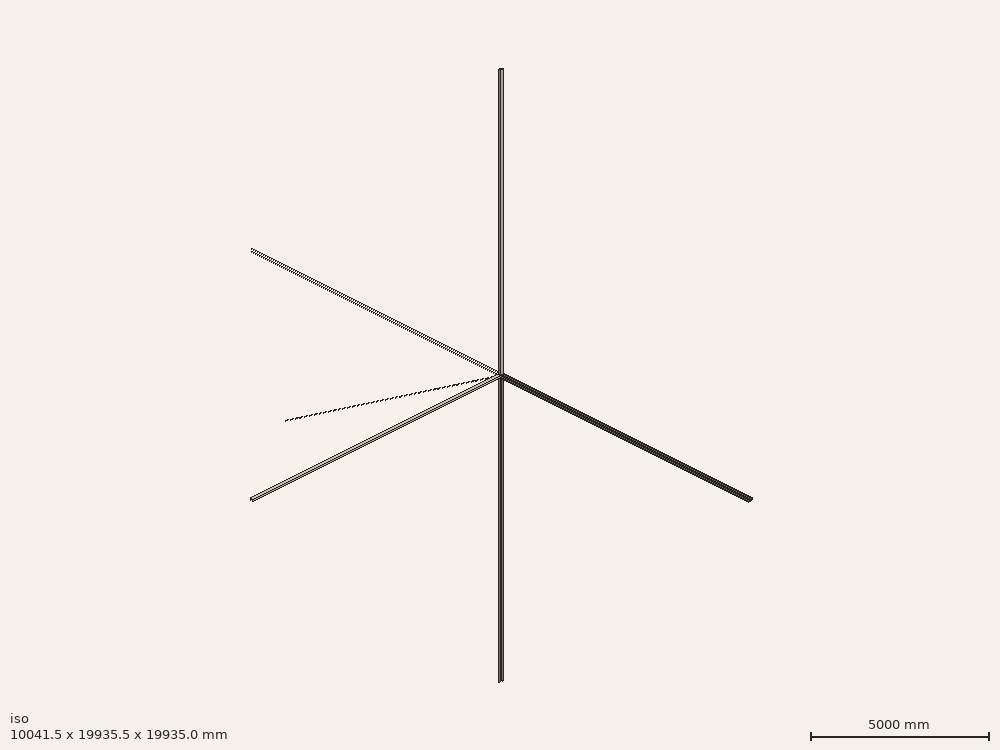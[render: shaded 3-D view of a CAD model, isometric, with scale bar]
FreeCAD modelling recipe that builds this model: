
FCSTD DOCUMENT  (FreeCAD 0.15R4671 (Git))
Label: FullGraphicDisplayBackCover
License: All rights reserved
LicenseURL: http://en.wikipedia.org/wiki/All_rights_reserved
objects: Sketcher::SketchObject×18, PartDesign::Pocket×13, Part::Feature×5, PartDesign::Pad×5, PartDesign::Fillet×5, Mesh::Feature×1
note: 64 computed .brp shape members not serialized (recipe doc carries the construction recipe); baked Part::Feature solids carry a one-line shape summary decoded from their .brp

FEATURE [Mesh::Feature] geetech_graphic_smart_controller
  Placement = pos=(47,-58,-38) rot=(0.447214,-0.447214,0.774597;1.82349rad)
FEATURE [Part::Feature] Part__Feature  label="FrontCover"
  Placement = pos=(0,-37,0) rot=(0,0,1;0rad)
  shape: bbox 100.5 x 70 x 100 mm, 43 faces (baked)
FEATURE [Part::Feature] Part__Feature001  label="OB1515_180mm"
  Placement = pos=(-88,7.5,50) rot=(0,1,0;1.5708rad)
  shape: bbox 180 x 15 x 15 mm, 158 faces (baked)
FEATURE [Part::Feature] Part__Feature002  label="OB1515_180mm001"
  Placement = pos=(-88,7.5,-50) rot=(0,1,0;1.5708rad)
  shape: bbox 180 x 15 x 15 mm, 158 faces (baked)
FEATURE [Sketcher::SketchObject] Sketch
  Placement = pos=(0,0,0) rot=(-1,0,0;4.71239rad)
  sketch-geometry (4):
    g0: LineSegment StartX=-60 StartY=57.5 StartZ=0 EndX=60 EndY=57.5 EndZ=0
    g1: LineSegment StartX=60 StartY=57.5 StartZ=0 EndX=60 EndY=-57.5 EndZ=0
    g2: LineSegment StartX=60 StartY=-57.5 StartZ=0 EndX=-60 EndY=-57.5 EndZ=0
    g3: LineSegment StartX=-60 StartY=-57.5 StartZ=0 EndX=-60 EndY=57.5 EndZ=0
  constraints (12):
    c: Coincident(g0,g1)
    c: Coincident(g1,g2)
    c: Coincident(g2,g3)
    c: Coincident(g3,g0)
    c: Horizontal(g0)
    c: Horizontal(g2)
    c: Vertical(g1)
    c: Vertical(g3)
    c: DistanceY(g1,g0) = 115
    c: DistanceY(g-1,g0) = 57.5
    c: DistanceX(g1,g2) = -120
    c: DistanceX(g-1,g2) = -60
FEATURE [PartDesign::Pad] Pad
  Length = 65
  Length2 = 100
  Placement = pos=(0,0,0) rot=(-1,0,0;4.71239rad)
  Sketch = -> Sketch
  Type = 0
FEATURE [Sketcher::SketchObject] Sketch001
  Placement = pos=(0,-65,0) rot=(1,0,0;1.5708rad)
  Support = -> Pad [Face6]
  sketch-geometry (8):
    g0: LineSegment StartX=50.5 StartY=42.5 StartZ=0 EndX=60.5 EndY=42.5 EndZ=0
    g1: LineSegment StartX=60.5 StartY=42.5 StartZ=0 EndX=60.5 EndY=-42.5 EndZ=0
    g2: LineSegment StartX=60.5 StartY=-42.5 StartZ=0 EndX=50.5 EndY=-42.5 EndZ=0
    g3: LineSegment StartX=50.5 StartY=-42.5 StartZ=0 EndX=50.5 EndY=42.5 EndZ=0
    g4: LineSegment StartX=-60.75 StartY=42.5 StartZ=0 EndX=-50 EndY=42.5 EndZ=0
    g5: LineSegment StartX=-50 StartY=42.5 StartZ=0 EndX=-50 EndY=-42.5 EndZ=0
    g6: LineSegment StartX=-50 StartY=-42.5 StartZ=0 EndX=-60.75 EndY=-42.5 EndZ=0
    g7: LineSegment StartX=-60.75 StartY=-42.5 StartZ=0 EndX=-60.75 EndY=42.5 EndZ=0
  constraints (16):
    c: Coincident(g0,g1)
    c: Coincident(g1,g2)
    c: Coincident(g2,g3)
    c: Coincident(g3,g0)
    c: Horizontal(g0)
    c: Horizontal(g2)
    c: Vertical(g1)
    c: Vertical(g3)
    c: Coincident(g4,g5)
    c: Coincident(g5,g6)
    c: Coincident(g6,g7)
    c: Coincident(g7,g4)
    c: Horizontal(g4)
    c: Horizontal(g6)
    c: Vertical(g5)
    c: Vertical(g7)
FEATURE [PartDesign::Pocket] Pocket
  Length = 5
  Placement = pos=(0,0,0) rot=(-1,0,0;4.71239rad)
  Sketch = -> Sketch001
  Type = 1
FEATURE [Sketcher::SketchObject] Sketch002
  Placement = pos=(60,0,0) rot=(0.707107,0,0.707107;3.14159rad)
  Support = -> Pocket [Face3]
  sketch-geometry (5):
    g0: LineSegment StartX=-50.25 StartY=66.5 StartZ=0 EndX=-50 EndY=65 EndZ=0
    g1: LineSegment StartX=-50 StartY=65 StartZ=0 EndX=50 EndY=7 EndZ=0
    g2: LineSegment StartX=50 StartY=7 StartZ=0 EndX=58.1349 EndY=7 EndZ=0
    g3: LineSegment StartX=58.1349 StartY=7 StartZ=0 EndX=59.3034 EndY=76.0691 EndZ=0
    g4: LineSegment StartX=59.3034 StartY=76.0691 StartZ=0 EndX=-50.25 EndY=66.5 EndZ=0
  constraints (5):
    c: Coincident(g0,g1)
    c: Coincident(g1,g2)
    c: Coincident(g2,g3)
    c: Coincident(g3,g4)
    c: Coincident(g0,g4)
FEATURE [PartDesign::Pocket] Pocket001
  Length = 5
  Placement = pos=(0,0,0) rot=(-1,0,0;4.71239rad)
  Sketch = -> Sketch002
  Type = 1
FEATURE [Sketcher::SketchObject] Sketch003
  Placement = pos=(0,0,57.5) rot=(0,0,1;3.14159rad)
  Support = -> Pocket001 [Face1]
  sketch-geometry (8):
    g0: LineSegment StartX=50 StartY=77.5 StartZ=0 EndX=60.5 EndY=77.5 EndZ=0
    g1: LineSegment StartX=60.5 StartY=77.5 StartZ=0 EndX=60.5 EndY=7 EndZ=0
    g2: LineSegment StartX=60.5 StartY=7 StartZ=0 EndX=50 EndY=7 EndZ=0
    g3: LineSegment StartX=50 StartY=7 StartZ=0 EndX=50 EndY=77.5 EndZ=0
    g4: LineSegment StartX=-61.25 StartY=77.6703 StartZ=0 EndX=-50.5 EndY=77.6703 EndZ=0
    g5: LineSegment StartX=-50.5 StartY=77.6703 StartZ=0 EndX=-50.5 EndY=7 EndZ=0
    g6: LineSegment StartX=-50.5 StartY=7 StartZ=0 EndX=-61.25 EndY=7 EndZ=0
    g7: LineSegment StartX=-61.25 StartY=7 StartZ=0 EndX=-61.25 EndY=77.6703 EndZ=0
  constraints (16):
    c: Coincident(g0,g1)
    c: Coincident(g1,g2)
    c: Coincident(g2,g3)
    c: Coincident(g3,g0)
    c: Horizontal(g0)
    c: Horizontal(g2)
    c: Vertical(g1)
    c: Vertical(g3)
    c: Coincident(g4,g5)
    c: Coincident(g5,g6)
    c: Coincident(g6,g7)
    c: Coincident(g7,g4)
    c: Horizontal(g4)
    c: Horizontal(g6)
    c: Vertical(g5)
    c: Vertical(g7)
FEATURE [PartDesign::Pocket] Pocket002
  Length = 5
  Placement = pos=(0,0,0) rot=(-1,0,0;4.71239rad)
  Sketch = -> Sketch003
  Type = 1
FEATURE [Sketcher::SketchObject] Sketch004
  Placement = pos=(50.5,0,0) rot=(0.707107,0,0.707107;3.14159rad)
  Support = -> Pocket002 [Face17]
  sketch-geometry (4):
    g0: LineSegment StartX=-58 StartY=65.5 StartZ=0 EndX=-50 EndY=65.5 EndZ=0
    g1: LineSegment StartX=-50 StartY=65.5 StartZ=0 EndX=-50 EndY=7 EndZ=0
    g2: LineSegment StartX=-50 StartY=7 StartZ=0 EndX=-58 EndY=7 EndZ=0
    g3: LineSegment StartX=-58 StartY=7 StartZ=0 EndX=-58 EndY=65.5 EndZ=0
  constraints (8):
    c: Coincident(g0,g1)
    c: Coincident(g1,g2)
    c: Coincident(g2,g3)
    c: Coincident(g3,g0)
    c: Horizontal(g0)
    c: Horizontal(g2)
    c: Vertical(g1)
    c: Vertical(g3)
FEATURE [PartDesign::Pocket] Pocket003
  Length = 5
  Placement = pos=(0,0,0) rot=(-1,0,0;4.71239rad)
  Sketch = -> Sketch004
  Type = 1
FEATURE [Sketcher::SketchObject] Sketch005
  Placement = pos=(0,0,0) rot=(-1,0,0;1.5708rad)
  Support = -> Pocket003 [Face2]
  sketch-geometry (4):
    g0: LineSegment StartX=-47 StartY=42.5 StartZ=0 EndX=47.5 EndY=42.5 EndZ=0
    g1: LineSegment StartX=47.5 StartY=42.5 StartZ=0 EndX=47.5 EndY=-42.5 EndZ=0
    g2: LineSegment StartX=47.5 StartY=-42.5 StartZ=0 EndX=-47 EndY=-42.5 EndZ=0
    g3: LineSegment StartX=-47 StartY=-42.5 StartZ=0 EndX=-47 EndY=42.5 EndZ=0
  constraints (8):
    c: Coincident(g0,g1)
    c: Coincident(g1,g2)
    c: Coincident(g2,g3)
    c: Coincident(g3,g0)
    c: Horizontal(g0)
    c: Horizontal(g2)
    c: Vertical(g1)
    c: Vertical(g3)
FEATURE [PartDesign::Pocket] Pocket004
  Length = 5
  Placement = pos=(0,0,0) rot=(-1,0,0;4.71239rad)
  Sketch = -> Sketch005
  Type = 1
FEATURE [Sketcher::SketchObject] Sketch006
  Placement = pos=(47.5,0,0) rot=(0.707107,0,-0.707107;3.14159rad)
  Support = -> Pocket004 [Face18]
  sketch-geometry (4):
    g0: LineSegment StartX=14.7798 StartY=44.7511 StartZ=0 EndX=16.486 EndY=41.7608 EndZ=0
    g1: LineSegment StartX=16.486 StartY=41.7608 StartZ=0 EndX=-7.74724 EndY=27.9339 EndZ=0
    g2: LineSegment StartX=-7.74724 StartY=27.9339 StartZ=0 EndX=-9.45343 EndY=30.9242 EndZ=0
    g3: LineSegment StartX=-9.45343 StartY=30.9242 StartZ=0 EndX=14.7798 EndY=44.7511 EndZ=0
  constraints (7):
    c: Coincident(g0,g1)
    c: Coincident(g1,g2)
    c: Coincident(g2,g3)
    c: Angle(g1,g2) = 1.5708
    c: Angle(g2,g3) = 1.5708
    c: Coincident(g0,g3)
    c: Angle(g3,g0) = 1.5708
FEATURE [PartDesign::Pocket] Pocket005
  Length = 5
  Placement = pos=(0,0,0) rot=(-1,0,0;4.71239rad)
  Sketch = -> Sketch006
  Type = 0
FEATURE [Sketcher::SketchObject] Sketch007
  Placement = pos=(0,0,-42.5) rot=(0,0,1;3.14159rad)
  Support = -> Pocket005 [Face17]
  sketch-geometry (4):
    g0: LineSegment StartX=-45 StartY=60 StartZ=0 EndX=45 EndY=60 EndZ=0
    g1: LineSegment StartX=45 StartY=60 StartZ=0 EndX=45 EndY=73.3448 EndZ=0
    g2: LineSegment StartX=45 StartY=73.3448 StartZ=0 EndX=-45 EndY=73.3448 EndZ=0
    g3: LineSegment StartX=-45 StartY=73.3448 StartZ=0 EndX=-45 EndY=60 EndZ=0
  constraints (8):
    c: Coincident(g0,g1)
    c: Coincident(g1,g2)
    c: Coincident(g2,g3)
    c: Coincident(g3,g0)
    c: Horizontal(g0)
    c: Horizontal(g2)
    c: Vertical(g1)
    c: Vertical(g3)
FEATURE [PartDesign::Pad] Pad001
  Length = 4.3
  Length2 = 100
  Placement = pos=(0,0,0) rot=(-1,0,0;4.71239rad)
  Reversed = true
  Sketch = -> Sketch007
  Type = 0
FEATURE [PartDesign::Fillet] Fillet
  Base = -> Pad001 [Edge92,Edge88]
  Placement = pos=(0,0,0) rot=(-1,0,0;4.71239rad)
  Radius = 2
FEATURE [Sketcher::SketchObject] Sketch008
  Placement = pos=(0,0,0) rot=(-1,0,0;1.5708rad)
  Support = -> Fillet [Face10]
  sketch-geometry (4):
    g0: LineSegment StartX=-49 StartY=44 StartZ=0 EndX=50 EndY=44 EndZ=0
    g1: LineSegment StartX=50 StartY=44 StartZ=0 EndX=50 EndY=-43 EndZ=0
    g2: LineSegment StartX=50 StartY=-43 StartZ=0 EndX=-49 EndY=-43 EndZ=0
    g3: LineSegment StartX=-49 StartY=-43 StartZ=0 EndX=-49 EndY=44 EndZ=0
  constraints (8):
    c: Coincident(g0,g1)
    c: Coincident(g1,g2)
    c: Coincident(g2,g3)
    c: Coincident(g3,g0)
    c: Horizontal(g0)
    c: Horizontal(g2)
    c: Vertical(g1)
    c: Vertical(g3)
FEATURE [PartDesign::Pad] Pad002
  Length = 3
  Length2 = 100
  Placement = pos=(0,0,0) rot=(-1,0,0;4.71239rad)
  Reversed = true
  Sketch = -> Sketch008
  Type = 0
FEATURE [Sketcher::SketchObject] Sketch009
  Placement = pos=(0,-26.938,15.6241) rot=(1,0,0;1.04521rad)
  Support = -> Pad002 [Face4]
  sketch-geometry (10):
    g0: ArcOfCircle CenterX=-43.5 CenterY=25.5 CenterZ=0 NormalX=0 NormalY=0 NormalZ=1 Radius=6 StartAngle=4.71239 EndAngle=6.28319
    g1: ArcOfCircle CenterX=44.5 CenterY=25.5 CenterZ=0 NormalX=0 NormalY=0 NormalZ=1 Radius=6 StartAngle=3.14434 EndAngle=4.70541
    g2: LineSegment StartX=38.5 StartY=25.4835 StartZ=0 EndX=38.5 EndY=36 EndZ=0
    g3: LineSegment StartX=38.5 StartY=36 StartZ=0 EndX=48.5 EndY=36 EndZ=0
    g4: LineSegment StartX=48.5 StartY=36 StartZ=0 EndX=48.5 EndY=19.5 EndZ=0
    g5: LineSegment StartX=48.5 StartY=19.5 StartZ=0 EndX=44.4581 EndY=19.5001 EndZ=0
    g6: LineSegment StartX=-37.5 StartY=25.5 StartZ=0 EndX=-37.5 EndY=37.5 EndZ=0
    g7: LineSegment StartX=-37.5 StartY=37.5 StartZ=0 EndX=-47.5 EndY=37.5 EndZ=0
    g8: LineSegment StartX=-47.5 StartY=37.5 StartZ=0 EndX=-47.5 EndY=19.5 EndZ=0
    g9: LineSegment StartX=-47.5 StartY=19.5 StartZ=0 EndX=-43.5 EndY=19.5 EndZ=0
  constraints (16):
    c: Radius(g0) = 6
    c: Radius(g1) = 6
    c: Coincident(g2,g3)
    c: Coincident(g3,g4)
    c: Coincident(g4,g5)
    c: Coincident(g6,g7)
    c: Coincident(g7,g8)
    c: Coincident(g8,g9)
    c: Coincident(g1,g5)
    c: Coincident(g1,g2)
    c: Coincident(g0,g6)
    c: Coincident(g0,g9)
    c: Horizontal(g7)
    c: Vertical(g8)
    c: Horizontal(g3)
    c: Vertical(g4)
FEATURE [PartDesign::Pad] Pad003
  Length = 20
  Length2 = 100
  Placement = pos=(0,0,0) rot=(-1,0,0;4.71239rad)
  Reversed = true
  Sketch = -> Sketch009
  Type = 0
FEATURE [Sketcher::SketchObject] Sketch010
  Placement = pos=(0,0,57.5) rot=(0,0,1;3.14159rad)
  Support = -> Pad003 [Face29]
  sketch-geometry (4):
    g0: LineSegment StartX=-61 StartY=0 StartZ=0 EndX=61 EndY=0 EndZ=0
    g1: LineSegment StartX=61 StartY=0 StartZ=0 EndX=61 EndY=-16 EndZ=0
    g2: LineSegment StartX=61 StartY=-16 StartZ=0 EndX=-61 EndY=-16 EndZ=0
    g3: LineSegment StartX=-61 StartY=-16 StartZ=0 EndX=-61 EndY=0 EndZ=0
  constraints (8):
    c: Coincident(g0,g1)
    c: Coincident(g1,g2)
    c: Coincident(g2,g3)
    c: Coincident(g3,g0)
    c: Horizontal(g0)
    c: Horizontal(g2)
    c: Vertical(g1)
    c: Vertical(g3)
FEATURE [PartDesign::Pocket] Pocket006
  Length = 5
  Placement = pos=(0,0,0) rot=(-1,0,0;4.71239rad)
  Sketch = -> Sketch010
  Type = 1
FEATURE [Part::Feature] Pocket007
  shape: bbox 120 x 73.36 x 115 mm, 37 faces (baked)
FEATURE [Sketcher::SketchObject] Sketch011
  Placement = pos=(0,-26.938,15.6241) rot=(1,0,0;1.04521rad)
  Support = -> Pocket007 [Face4]
  sketch-geometry (10):
    g0: ArcOfCircle CenterX=-43.5 CenterY=25.5 CenterZ=0 NormalX=0 NormalY=0 NormalZ=1 Radius=6 StartAngle=4.71239 EndAngle=6.28319
    g1: ArcOfCircle CenterX=44.5 CenterY=25.5 CenterZ=0 NormalX=0 NormalY=0 NormalZ=1 Radius=6 StartAngle=3.14159 EndAngle=4.71239
    g2: LineSegment StartX=-43.5 StartY=19.5 StartZ=0 EndX=-47 EndY=19.5 EndZ=0
    g3: LineSegment StartX=-47 StartY=19.5 StartZ=0 EndX=-47 EndY=31 EndZ=0
    g4: LineSegment StartX=-47 StartY=31 StartZ=0 EndX=-37.5 EndY=31 EndZ=0
    g5: LineSegment StartX=-37.5 StartY=31 StartZ=0 EndX=-37.5 EndY=25.5 EndZ=0
    g6: LineSegment StartX=44.5 StartY=19.5 StartZ=0 EndX=47.5 EndY=19.5 EndZ=0
    g7: LineSegment StartX=47.5 StartY=19.5 StartZ=0 EndX=47.5 EndY=31 EndZ=0
    g8: LineSegment StartX=47.5 StartY=31 StartZ=0 EndX=38.5 EndY=31 EndZ=0
    g9: LineSegment StartX=38.5 StartY=31 StartZ=0 EndX=38.5 EndY=25.5 EndZ=0
  constraints (10):
    c: Coincident(g2,g3)
    c: Coincident(g3,g4)
    c: Coincident(g4,g5)
    c: Coincident(g6,g7)
    c: Coincident(g7,g8)
    c: Coincident(g8,g9)
    c: Coincident(g1,g6)
    c: Coincident(g1,g9)
    c: Coincident(g0,g5)
    c: Coincident(g0,g2)
FEATURE [PartDesign::Pad] Pad004
  Length = 4.6
  Length2 = 100
  Sketch = -> Sketch011
  Type = 0
FEATURE [Sketcher::SketchObject] Sketch012
  Placement = pos=(0,-30.9172,17.932) rot=(1,0,0;1.04521rad)
  Support = -> Pad004 [Face30]
  sketch-geometry (2):
    g0: Circle CenterX=-43.5 CenterY=25.5 CenterZ=0 NormalX=0 NormalY=0 NormalZ=1 Radius=1.8
    g1: Circle CenterX=44.5 CenterY=25.5 CenterZ=0 NormalX=0 NormalY=0 NormalZ=1 Radius=1.8
  constraints (2):
    c: Radius(g0) = 1.8
    c: Equal(g0,g1)
FEATURE [PartDesign::Pocket] Pocket008
  Length = 5
  Sketch = -> Sketch012
  Type = 1
FEATURE [Sketcher::SketchObject] Sketch013
  Placement = pos=(0,-26.938,15.6241) rot=(1,0,0;1.04521rad)
  Support = -> Pocket008 [Face4]
  sketch-geometry (2):
    g0: Circle CenterX=-43.5 CenterY=25.5 CenterZ=0 NormalX=0 NormalY=0 NormalZ=1 Radius=3.45
    g1: Circle CenterX=44.5 CenterY=25.5 CenterZ=0 NormalX=0 NormalY=0 NormalZ=1 Radius=3.45
  constraints (2):
    c: Radius(g0) = 3.45
    c: Equal(g0,g1)
FEATURE [PartDesign::Pocket] Pocket009
  Length = 5
  Sketch = -> Sketch013
  Type = 1
FEATURE [Sketcher::SketchObject] Sketch014
  Placement = pos=(0,-7,0) rot=(1,0,0;1.5708rad)
  Support = -> Pocket009 [Face23]
  sketch-geometry (4):
    g0: Circle CenterX=55 CenterY=50 CenterZ=0 NormalX=0 NormalY=0 NormalZ=1 Radius=1.8
    g1: Circle CenterX=-55 CenterY=50 CenterZ=0 NormalX=0 NormalY=0 NormalZ=1 Radius=1.8
    g2: Circle CenterX=55 CenterY=-50 CenterZ=0 NormalX=0 NormalY=0 NormalZ=1 Radius=1.8
    g3: Circle CenterX=-55 CenterY=-50 CenterZ=0 NormalX=0 NormalY=0 NormalZ=1 Radius=1.8
  constraints (4):
    c: Radius(g1) = 1.8
    c: Equal(g1,g0)
    c: Equal(g1,g2)
    c: Equal(g1,g3)
FEATURE [PartDesign::Pocket] Pocket010
  Length = 5
  Sketch = -> Sketch014
  Type = 1
FEATURE [Sketcher::SketchObject] Sketch015
  Placement = pos=(0,-7,0) rot=(1,0,0;1.5708rad)
  Support = -> Pocket010 [Face34]
  sketch-geometry (4):
    g0: Circle CenterX=-55 CenterY=-50 CenterZ=0 NormalX=0 NormalY=0 NormalZ=1 Radius=3.6
    g1: Circle CenterX=55 CenterY=-50 CenterZ=0 NormalX=0 NormalY=0 NormalZ=1 Radius=3.6
    g2: Circle CenterX=55 CenterY=50 CenterZ=0 NormalX=0 NormalY=0 NormalZ=1 Radius=3.6
    g3: Circle CenterX=-55 CenterY=50 CenterZ=0 NormalX=0 NormalY=0 NormalZ=1 Radius=3.6
  constraints (4):
    c: Radius(g3) = 3.6
    c: Equal(g3,g2)
    c: Equal(g3,g1)
    c: Equal(g3,g0)
FEATURE [PartDesign::Pocket] Pocket011
  Length = 3
  Sketch = -> Sketch015
  Type = 0
FEATURE [PartDesign::Fillet] Fillet001
  Base = -> Pocket011 [Edge124,Edge159,Edge141,Edge167,Edge166,Edge165,Edge160,Edge158]
  Radius = 4
FEATURE [PartDesign::Fillet] Fillet002
  Base = -> Fillet001 [Edge7,Edge101]
  Radius = 1
FEATURE [PartDesign::Fillet] Fillet003
  Base = -> Fillet002 [Edge21,Edge68]
  Radius = 2
FEATURE [Part::Feature] Fillet004  label="FullGraphicDisplayBackCover_noCableHole"
  shape: bbox 120.7 x 77.07 x 115.7 mm, 93 faces (baked)
FEATURE [Sketcher::SketchObject] Sketch016
  Placement = pos=(0,0,0) rot=(0,0.707107,0.707107;3.14159rad)
  Support = -> Fillet004 [Face7]
  sketch-geometry (4):
    g0: LineSegment StartX=-1.52962 StartY=6 StartZ=0 EndX=38.4704 EndY=6 EndZ=0
    g1: LineSegment StartX=38.4704 StartY=6 StartZ=0 EndX=38.4704 EndY=-6 EndZ=0
    g2: LineSegment StartX=38.4704 StartY=-6 StartZ=0 EndX=-1.52962 EndY=-6 EndZ=0
    g3: LineSegment StartX=-1.52962 StartY=-6 StartZ=0 EndX=-1.52962 EndY=6 EndZ=0
  constraints (10):
    c: Coincident(g0,g1)
    c: Coincident(g1,g2)
    c: Coincident(g2,g3)
    c: Coincident(g3,g0)
    c: Horizontal(g0)
    c: Horizontal(g2)
    c: Vertical(g1)
    c: Vertical(g3)
    c: DistanceY(g1,g0) = 12
    c: DistanceX(g0,g0) = -40
FEATURE [PartDesign::Pocket] Pocket012
  Length = 5
  Sketch = -> Sketch016
  Type = 0
FEATURE [PartDesign::Fillet] Fillet005  label="FullGraphicDisplayBackCover_x"
  Base = -> Pocket012 [Edge218,Edge216,Edge219,Edge221]
  Radius = 2
FEATURE [Sketcher::SketchObject] Sketch017
  Placement = pos=(0,0,-46.8) rot=(1,0,0;3.14159rad)
  Support = -> Fillet005 [Face85]
  sketch-geometry (1):
    g0: Circle CenterX=0 CenterY=69 CenterZ=0 NormalX=0 NormalY=0 NormalZ=1 Radius=1.5
  constraints (1):
    c: Radius(g0) = 1.5
FEATURE [PartDesign::Pocket] Pocket013  label="FullGraphicDisplayBackCover"
  Length = 5
  Sketch = -> Sketch017
  Type = 0
